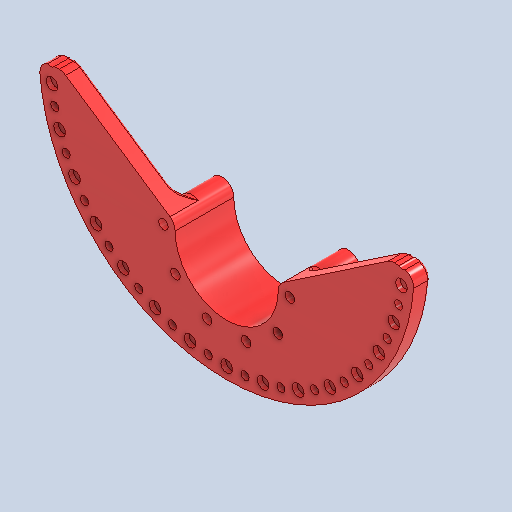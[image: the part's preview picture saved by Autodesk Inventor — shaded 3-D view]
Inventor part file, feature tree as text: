
AUTODESK INVENTOR PART (.ipt)
format: ipt  version: 2024 (Build 280153000, 153)  size: 428,544 bytes
history: native  units: mm
features: sketch x5, fillet x4, hole x3, pattern_circular x3, extrude x2, other x1, projected_geometry x1
ambient origin geometry x8: Origin, YZ Plane, XZ Plane, XY Plane, X Axis, Y Axis, Z Axis, Center Point
bodies: Body1 (feature_tree)
feature tree (19):
  other  "ソリッド1"
  extrude  "押し出し1"  Depth=160.0mm
  hole  "穴1"  [1 undecoded]
  pattern_circular  "円形状パターン1"  [2 undecoded]
  extrude  "押し出し2"  Depth=64.0mm
  hole  "穴2"  [1 undecoded]
  pattern_circular  "円形状パターン2"  [2 undecoded]
  fillet  "フィレット1"  Radius=7.0mm
  fillet  "フィレット2"  Radius=1.047198mm
  fillet  "フィレット3"  Radius=75.0mm
  fillet  "フィレット4"  Radius=300.0mm
  hole  "穴3"  [1 undecoded]
  pattern_circular  "円形状パターン3"  [2 undecoded]
  sketch  "スケッチ1"
  sketch  "スケッチ2"
  sketch  "スケッチ4"
  projected_geometry  "投影ループ2"
  sketch  "スケッチ5"
  sketch  "スケッチ6"
note: 9 required parameter values undecoded (feature->parameter linkage not recoverable at this tier; creation-order binding heuristic only, values carry confidence <= 0.55)
